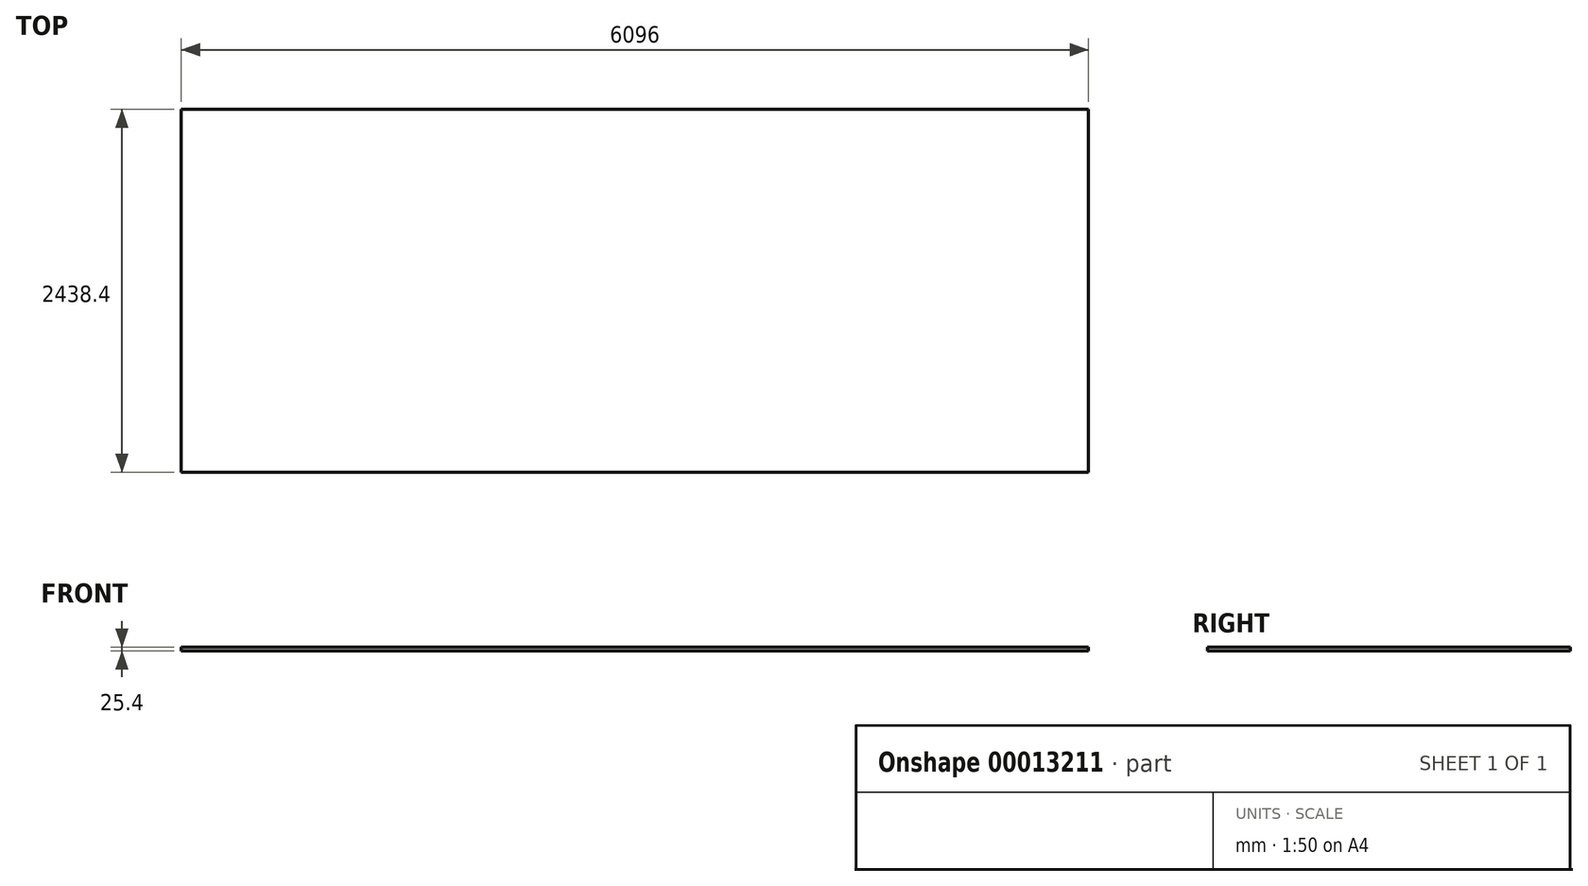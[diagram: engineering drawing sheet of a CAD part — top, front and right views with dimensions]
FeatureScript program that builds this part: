
annotation { "Feature Type Name" : "Feature", "Feature Type Description" : "" }
export const myFeature = defineFeature(function(context is Context, id is Id, definition is map)
    precondition{}
    {
        {
            var Q0;
            Q0=qCreatedBy(makeId("Top.planeOp"),FACE);
            var sketch = newSketch(context, id + "F0", { "sketchPlane" : qUnion([Q0])});
            skLineSegment(sketch, "E0.rect.bottom", {"start": v(3048, -1219.2) * mm, "end": v(-3048, -1219.2) * mm});
            skLineSegment(sketch, "E0.rect.top", {"start": v(3048, 1219.2) * mm, "end": v(-3048, 1219.2) * mm});
            skLineSegment(sketch, "E0.rect.left", {"start": v(3048, -1219.2) * mm, "end": v(3048, 1219.2) * mm});
            skLineSegment(sketch, "E0.rect.right", {"start": v(-3048, -1219.2) * mm, "end": v(-3048, 1219.2) * mm});
            skPoint(sketch, "E0.rect.middle", {"position": v(0, 0) * mm});
            skSolve(sketch);
        }
        {
            var Q0;
            Q0 = qSketchRegion(id + "F0", true);
            extrude(context, id + "F1", {"entities" : qUnion([Q0]), "depth" : 25.4 * mm});
        }
    });
